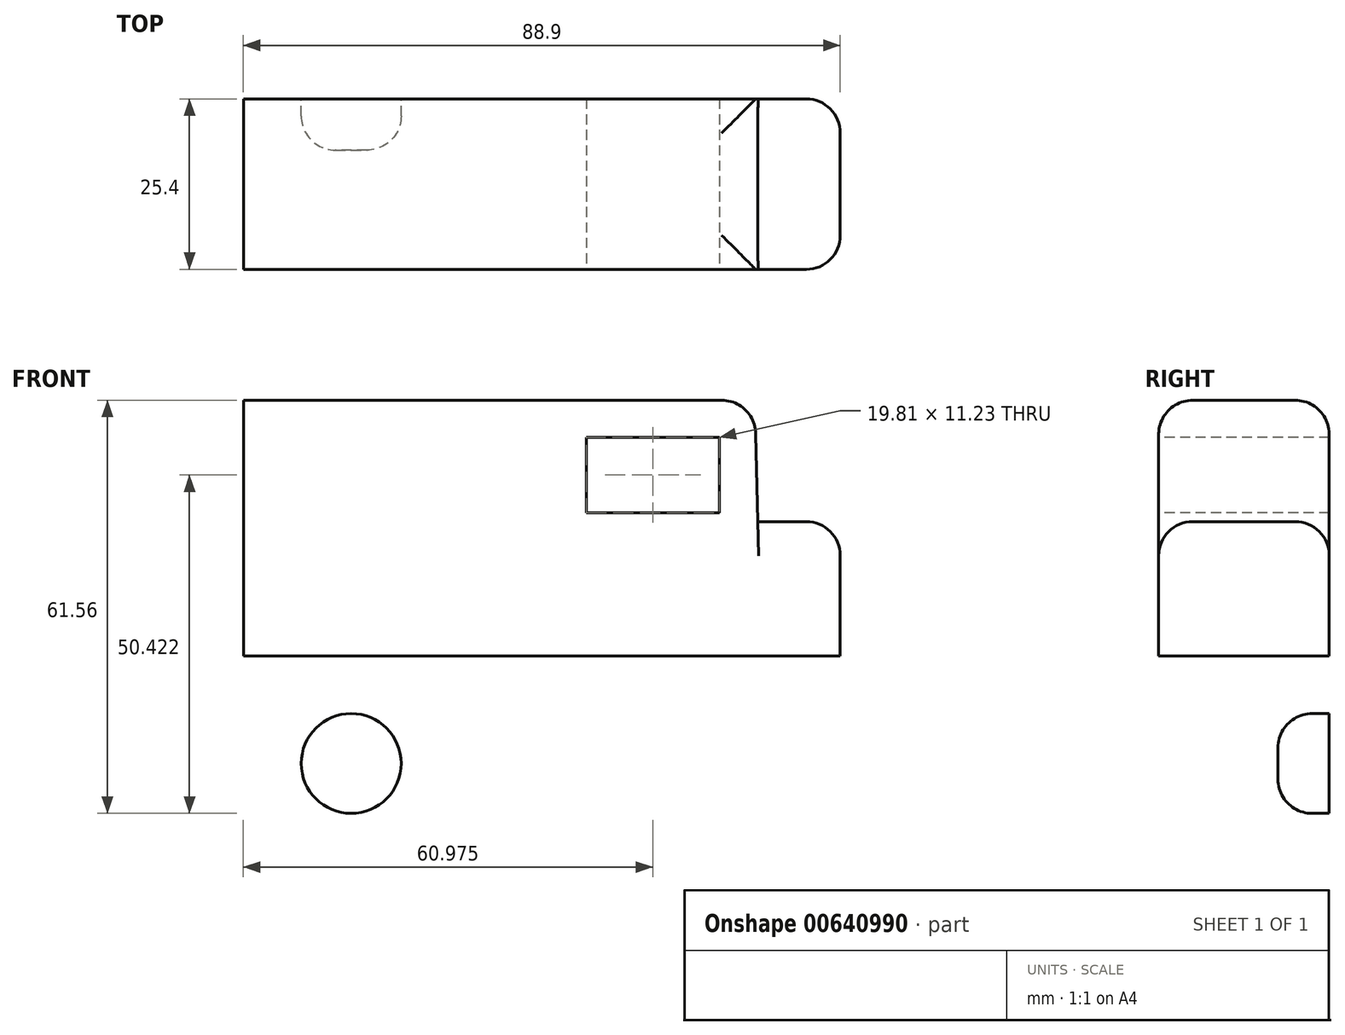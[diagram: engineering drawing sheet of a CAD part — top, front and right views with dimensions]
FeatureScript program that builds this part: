
annotation { "Feature Type Name" : "Feature", "Feature Type Description" : "" }
export const myFeature = defineFeature(function(context is Context, id is Id, definition is map)
    precondition{}
    {
        {
            var Q0;
            Q0=qCreatedBy(makeId("Front.planeOp"),FACE);
            var sketch = newSketch(context, id + "F0", { "sketchPlane" : qUnion([Q0])});
            skLineSegment(sketch, "E0", {"start": v(25.13, 35.9) * mm, "end": v(-51.07, 35.9) * mm});
            skLineSegment(sketch, "E1", {"start": v(-51.07, 35.9) * mm, "end": v(-51.07, -2.2) * mm});
            skLineSegment(sketch, "E2", {"start": v(-51.07, -2.2) * mm, "end": v(37.83, -2.2) * mm});
            skLineSegment(sketch, "E3", {"start": v(37.83, -2.2) * mm, "end": v(37.83, 17.83) * mm});
            skLineSegment(sketch, "E4", {"start": v(37.83, 17.83) * mm, "end": v(25.54, 17.83) * mm});
            skLineSegment(sketch, "E5", {"start": v(25.54, 17.83) * mm, "end": v(25.13, 35.9) * mm});
            skSolve(sketch);
        }
        {
            var Q0;
            Q0=makeQuery(id+"F0.imprint","IMPRINT",FACE,{"disambiguationData":[TD([[makeQuery(id+"F0.imprint","IMPRINT",EDGE,{"derivedFrom":sQuery(id+"F0.wireOp",EDGE,"E0")}),1.0]])]});
            extrude(context, id + "F1", {"entities" : qUnion([Q0]), "depth" : 25.4 * mm, "offsetDistance" : 25.4 * mm});
        }
        {
            var Q0;
            Q0=makeQuery(id+"F1.opExtrude","CAP_FACE",FACE,{"disambiguationData":[OSD([sQuery(id+"F0.wireOp",EDGE,"E0"),sQuery(id+"F0.wireOp",EDGE,"E1"),sQuery(id+"F0.wireOp",EDGE,"E2"),sQuery(id+"F0.wireOp",EDGE,"E3"),sQuery(id+"F0.wireOp",EDGE,"E4"),sQuery(id+"F0.wireOp",EDGE,"E5")])],"isStart":false});
            var sketch = newSketch(context, id + "F2", { "sketchPlane" : qUnion([Q0])});
            skLineSegment(sketch, "E6.bottom", {"start": v(19.8, 30.38) * mm, "end": v(0, 30.38) * mm});
            skLineSegment(sketch, "E6.top", {"start": v(19.8, 19.15) * mm, "end": v(0, 19.15) * mm});
            skLineSegment(sketch, "E6.left", {"start": v(19.8, 30.38) * mm, "end": v(19.8, 19.15) * mm});
            skLineSegment(sketch, "E6.right", {"start": v(0, 30.38) * mm, "end": v(0, 19.15) * mm});
            skSolve(sketch);
        }
        {
            var Q0;
            Q0 = qSketchRegion(id + "F2", true);
            extrude(context, id + "F3", {"entities" : qUnion([Q0]), "operationType" : NewBodyOperationType.REMOVE, "oppositeDirection" : true, "depth" : 25.4 * mm, "offsetDistance" : 25.4 * mm});
        }
        {
            var Q0;
            Q0=qCreatedBy(makeId("Front.planeOp"),FACE);
            var sketch = newSketch(context, id + "F4", { "sketchPlane" : qUnion([Q0])});
            skCircle(sketch, "E7", {"center": v(-35, -18.22) * mm, "radius": 7.44 * mm});
            skSolve(sketch);
        }
        {
            var Q0;
            Q0 = qSketchRegion(id + "F4", true);
            extrude(context, id + "F5", {"entities" : qUnion([Q0]), "depth" : 7.62 * mm, "offsetDistance" : 25.4 * mm});
        }
        {
            var Q0;
            Q0=makeQuery(id+"F5.opExtrude","CAP_EDGE",EDGE,{"disambiguationData":[OSD([sQuery(id+"F4.wireOp",EDGE,"E7")])],"isStart":false});
            fillet(context, id + "F6", {"entities" : qUnion([Q0]), "radius" : 5.08 * mm, "tangentPropagation" : true, "allowEdgeOverflow" : false});
        }
        {
            var Q0;
            Q0=makeQuery(id+"F1.opExtrude","SWEPT_EDGE",EDGE,{"disambiguationData":[OSD([sQuery(id+"F0.wireOp",EDGE,"E3"),sQuery(id+"F0.wireOp",EDGE,"E4")])]});
            var Q1;
            Q1=makeQuery(id+"F1.opExtrude","CAP_EDGE",EDGE,{"disambiguationData":[OSD([sQuery(id+"F0.wireOp",EDGE,"E0")])],"isStart":true});
            var Q2;
            Q2=makeQuery(id+"F1.opExtrude","SWEPT_EDGE",EDGE,{"disambiguationData":[OSD([sQuery(id+"F0.wireOp",EDGE,"E0"),sQuery(id+"F0.wireOp",EDGE,"E5")])]});
            var Q3;
            Q3=makeQuery(id+"F1.opExtrude","CAP_EDGE",EDGE,{"disambiguationData":[OSD([sQuery(id+"F0.wireOp",EDGE,"E0")])],"isStart":false});
            fillet(context, id + "F7", {"entities" : qUnion([Q0, Q1, Q2, Q3]), "radius" : 5.08 * mm, "tangentPropagation" : true, "allowEdgeOverflow" : false});
        }
        {
            var Q0;
            Q0=makeQuery(id+"F1.opExtrude","CAP_EDGE",EDGE,{"disambiguationData":[OSD([sQuery(id+"F0.wireOp",EDGE,"E3")])],"isStart":true});
            var Q1;
            Q1=makeQuery(id+"F1.opExtrude","CAP_EDGE",EDGE,{"disambiguationData":[OSD([sQuery(id+"F0.wireOp",EDGE,"E3")])],"isStart":false});
            fillet(context, id + "F8", {"entities" : qUnion([Q0, Q1]), "radius" : 5.08 * mm, "tangentPropagation" : true, "allowEdgeOverflow" : false});
        }
    });
